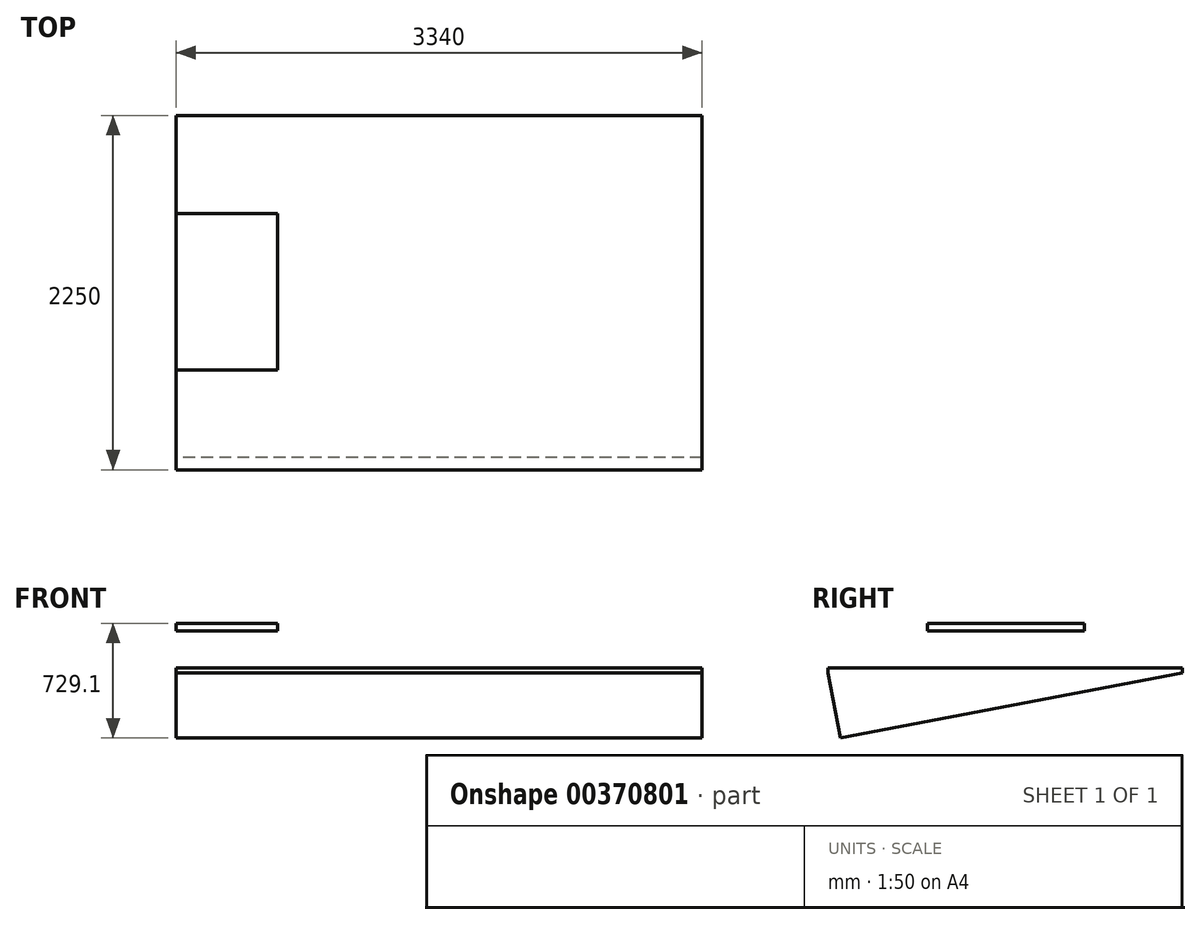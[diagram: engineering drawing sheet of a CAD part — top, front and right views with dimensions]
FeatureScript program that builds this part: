
annotation { "Feature Type Name" : "Feature", "Feature Type Description" : "" }
export const myFeature = defineFeature(function(context is Context, id is Id, definition is map)
    precondition{}
    {
        {
            var Q0;
            Q0=qCreatedBy(makeId("Right.planeOp"),FACE);
            var sketch = newSketch(context, id + "F0", { "sketchPlane" : qUnion([Q0])});
            skLineSegment(sketch, "E0.bottom", {"start": v(-495.58, 59.84) * mm, "end": v(499.42, 59.84) * mm});
            skLineSegment(sketch, "E0.top", {"start": v(-495.58, 9.84) * mm, "end": v(499.42, 9.84) * mm});
            skLineSegment(sketch, "E0.left", {"start": v(-495.58, 59.84) * mm, "end": v(-495.58, 9.84) * mm});
            skLineSegment(sketch, "E0.right", {"start": v(499.42, 59.84) * mm, "end": v(499.42, 9.84) * mm});
            skSolve(sketch);
        }
        {
            var Q0;
            Q0 = qSketchRegion(id + "F0", true);
            var Q1;
            Q1=makeQuery(id+"F0.imprint","IMPRINT",FACE,{"disambiguationData":[TD([[makeQuery(id+"F0.imprint","IMPRINT",EDGE,{"derivedFrom":sQuery(id+"F0.wireOp",EDGE,"E0.bottom")}),-1.0]])]});
            extrude(context, id + "F1", {"entities" : qUnion([Q0, Q1]), "depth" : 645 * mm});
        }
        {
            var Q0;
            Q0=qCreatedBy(makeId("Right.planeOp"),FACE);
            var sketch = newSketch(context, id + "F2", { "sketchPlane" : qUnion([Q0])});
            skLineSegment(sketch, "E1.bottom", {"start": v(-1128.34, -224.4) * mm, "end": v(1121.66, -224.4) * mm});
            skLineSegment(sketch, "E1.top", {"start": v(-1128.34, -254.4) * mm, "end": v(1121.66, -254.4) * mm});
            skLineSegment(sketch, "E1.left", {"start": v(-1128.34, -224.4) * mm, "end": v(-1128.34, -254.4) * mm});
            skLineSegment(sketch, "E1.right", {"start": v(1121.66, -224.4) * mm, "end": v(1121.66, -254.4) * mm});
            skLineSegment(sketch, "E2", {"start": v(-1128.34, -254.4) * mm, "end": v(-1049.06, -669.26) * mm});
            skLineSegment(sketch, "E3", {"start": v(-1049.06, -669.26) * mm, "end": v(-1049.06, -669.26) * mm});
            skLineSegment(sketch, "E4", {"start": v(-1049.06, -669.26) * mm, "end": v(1121.66, -254.4) * mm});
            skSolve(sketch);
        }
        {
            var Q0;
            Q0 = qSketchRegion(id + "F2", true);
            extrude(context, id + "F3", {"entities" : qUnion([Q0]), "depth" : 3340 * mm});
        }
    });
